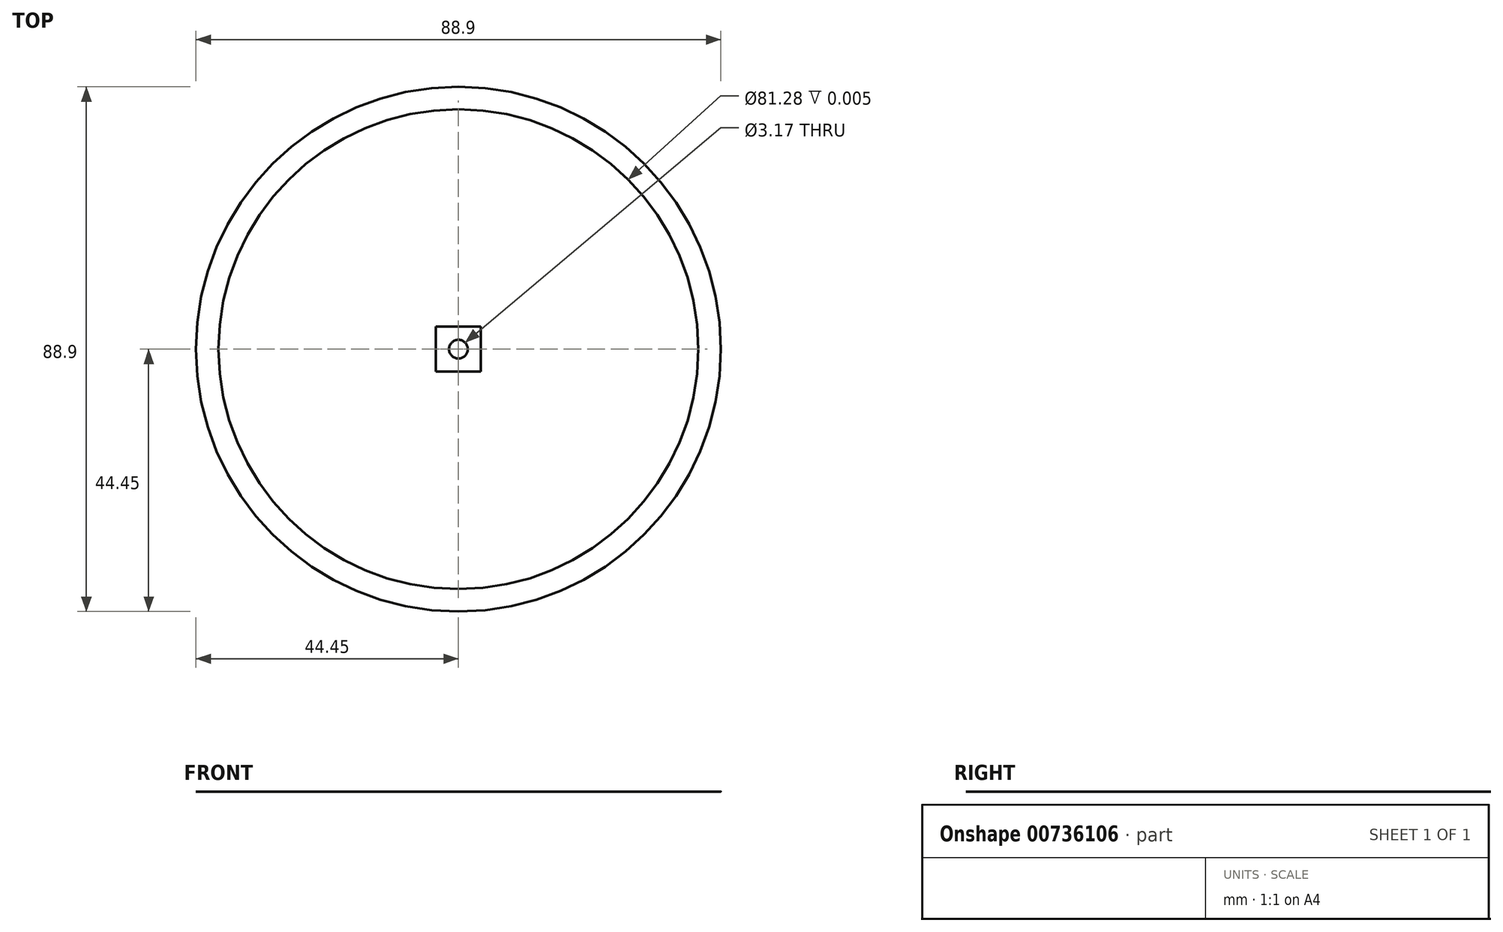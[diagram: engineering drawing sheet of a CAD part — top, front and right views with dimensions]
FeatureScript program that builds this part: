
annotation { "Feature Type Name" : "Feature", "Feature Type Description" : "" }
export const myFeature = defineFeature(function(context is Context, id is Id, definition is map)
    precondition{}
    {
        {
            var Q0;
            Q0=qCreatedBy(makeId("Top.planeOp"),FACE);
            var sketch = newSketch(context, id + "F0", { "sketchPlane" : qUnion([Q0])});
            skCircle(sketch, "E0", {"center": v(0, 0) * mm, "radius": 44.45 * mm});
            skCircle(sketch, "E1", {"center": v(0, 0) * mm, "radius": 40.64 * mm});
            skCircle(sketch, "E2", {"center": v(0, 0) * mm, "radius": 1.59 * mm});
            skLineSegment(sketch, "E3", {"start": v(-3.81, 0) * mm, "end": v(-3.81, -40.46) * mm});
            skLineSegment(sketch, "E4", {"start": v(-3.81, -40.46) * mm, "end": v(-3.81, 40.46) * mm});
            skLineSegment(sketch, "E5", {"start": v(3.81, 0) * mm, "end": v(3.81, -40.46) * mm});
            skLineSegment(sketch, "E6", {"start": v(3.81, -40.46) * mm, "end": v(3.81, 40.46) * mm});
            skLineSegment(sketch, "E7", {"start": v(0, -3.81) * mm, "end": v(40.46, -3.81) * mm});
            skLineSegment(sketch, "E8", {"start": v(40.46, -3.81) * mm, "end": v(-40.46, -3.81) * mm});
            skLineSegment(sketch, "E9", {"start": v(0, 3.81) * mm, "end": v(40.46, 3.81) * mm});
            skLineSegment(sketch, "E10", {"start": v(40.46, 3.81) * mm, "end": v(-40.46, 3.81) * mm});
            skSolve(sketch);
        }
        {
            var Q0;
            {var subQ0=sQuery(id+"F0.wireOp",EDGE,"E10");var subQ1=makeQuery(id+"F0.imprint","IMPRINT",VERTEX,{"derivedFrom":subQ0});Q0=makeQuery(id+"F0.imprint","IMPRINT",FACE,{"disambiguationData":[TD([[makeQuery(id+"F0.imprint","IMPRINT",EDGE,{"disambiguationData":[TD([[subQ1,1.0]])],"derivedFrom":subQ0}),-1.0]])]});}
            var Q1;
            {var subQ0=sQuery(id+"F0.wireOp",EDGE,"E4");var subQ1=makeQuery(id+"F0.imprint","IMPRINT",VERTEX,{"derivedFrom":subQ0});Q1=makeQuery(id+"F0.imprint","IMPRINT",FACE,{"disambiguationData":[TD([[makeQuery(id+"F0.imprint","IMPRINT",EDGE,{"disambiguationData":[TD([[subQ1,1.0]])],"derivedFrom":subQ0}),1.0]])]});}
            var Q2;
            {var subQ0=sQuery(id+"F0.wireOp",EDGE,"E6");var subQ1=makeQuery(id+"F0.imprint","IMPRINT",VERTEX,{"derivedFrom":subQ0});Q2=makeQuery(id+"F0.imprint","IMPRINT",FACE,{"disambiguationData":[TD([[makeQuery(id+"F0.imprint","IMPRINT",EDGE,{"disambiguationData":[TD([[subQ1,1.0]])],"derivedFrom":subQ0}),-1.0]])]});}
            var Q3;
            Q3=makeQuery(id+"F0.imprint","IMPRINT",FACE,{"disambiguationData":[TD([[makeQuery(id+"F0.imprint","IMPRINT",EDGE,{"derivedFrom":sQuery(id+"F0.wireOp",EDGE,"E2")}),-1.0]])]});
            var Q4;
            {var subQ0=sQuery(id+"F0.wireOp",EDGE,"E8");var subQ1=makeQuery(id+"F0.imprint","IMPRINT",VERTEX,{"derivedFrom":subQ0});Q4=makeQuery(id+"F0.imprint","IMPRINT",FACE,{"disambiguationData":[TD([[makeQuery(id+"F0.imprint","IMPRINT",EDGE,{"disambiguationData":[TD([[subQ1,1.0]])],"derivedFrom":subQ0}),1.0]])]});}
            var Q5;
            Q5=makeQuery(id+"F0.imprint","IMPRINT",FACE,{"disambiguationData":[TD([[makeQuery(id+"F0.imprint","IMPRINT",EDGE,{"derivedFrom":sQuery(id+"F0.wireOp",EDGE,"E0")}),1.0]])]});
            extrude(context, id + "F1", {"entities" : qUnion([Q0, Q1, Q2, Q3, Q4, Q5]), "depth" : 1 / 203.2 * mm, "offsetDistance" : 25.4 * mm});
        }
    });
